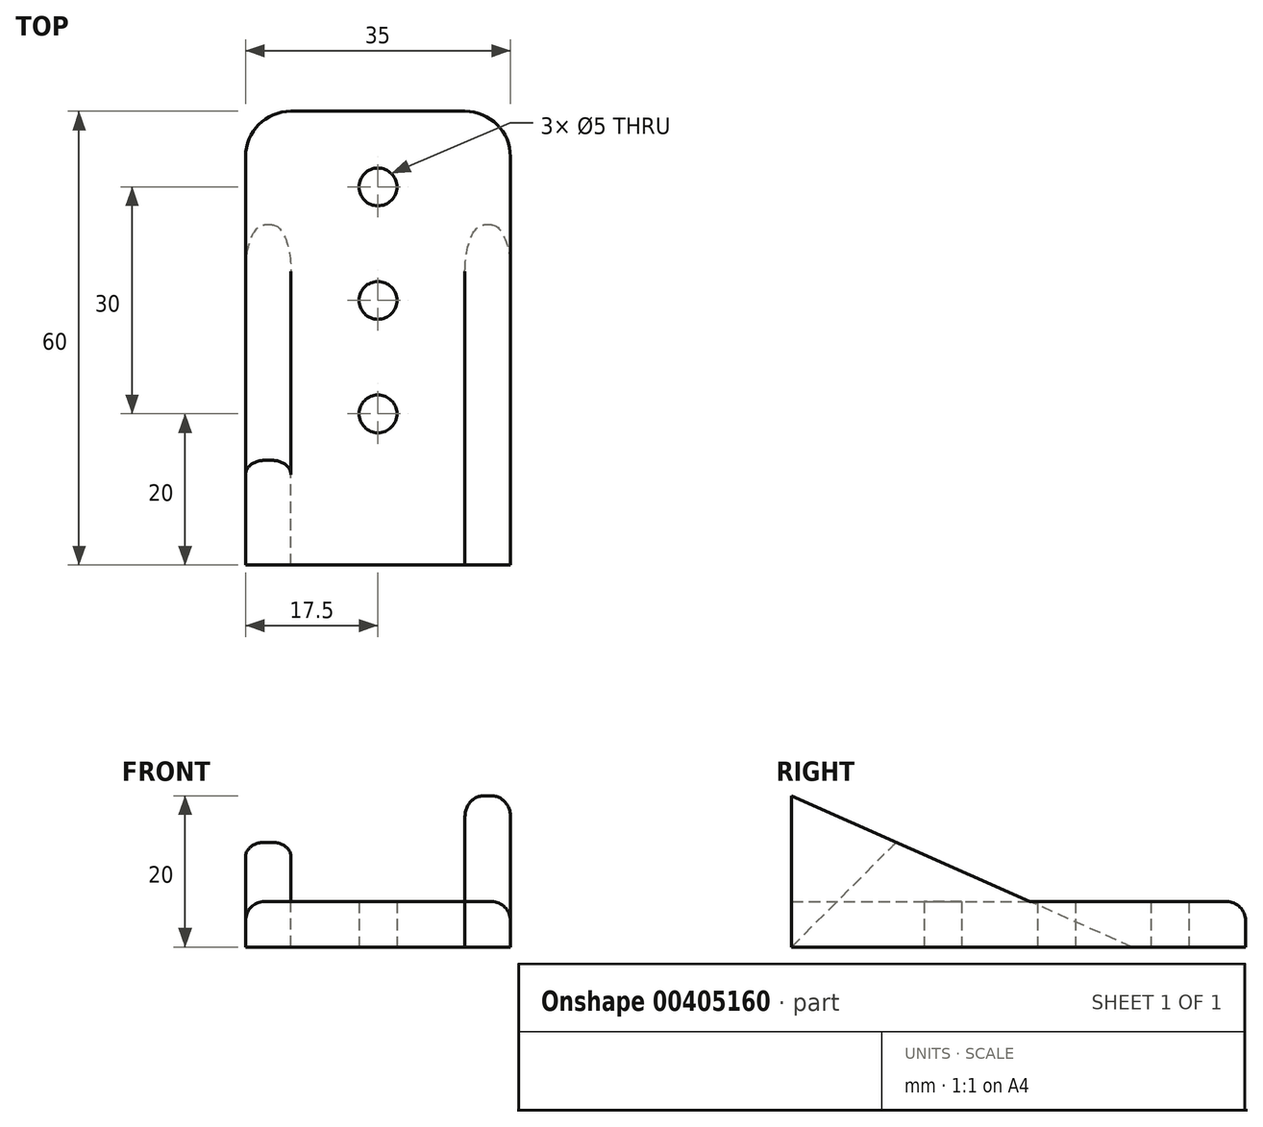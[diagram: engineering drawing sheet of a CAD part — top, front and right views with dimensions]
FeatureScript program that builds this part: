
annotation { "Feature Type Name" : "Feature", "Feature Type Description" : "" }
export const myFeature = defineFeature(function(context is Context, id is Id, definition is map)
    precondition{}
    {
        {
            var Q0;
            Q0=qCreatedBy(makeId("Top.planeOp"),FACE);
            var sketch = newSketch(context, id + "F0", { "sketchPlane" : qUnion([Q0])});
            skLineSegment(sketch, "E0.bottom", {"start": v(17.5, -30) * mm, "end": v(-17.5, -30) * mm});
            skLineSegment(sketch, "E0.top", {"start": v(17.5, 30) * mm, "end": v(-17.5, 30) * mm});
            skLineSegment(sketch, "E0.left", {"start": v(17.5, -30) * mm, "end": v(17.5, 30) * mm});
            skLineSegment(sketch, "E0.right", {"start": v(-17.5, -30) * mm, "end": v(-17.5, 30) * mm});
            skPoint(sketch, "E0.middle", {"position": v(0, 0) * mm});
            skLineSegment(sketch, "E1", {"start": v(0, 0) * mm, "end": v(0, 20) * mm});
            skLineSegment(sketch, "E2", {"start": v(0, 0) * mm, "end": v(0, -10) * mm});
            skCircle(sketch, "E3", {"center": v(0, 20) * mm, "radius": 2.5 * mm});
            skCircle(sketch, "E4", {"center": v(0, -10) * mm, "radius": 2.5 * mm});
            skLineSegment(sketch, "E5", {"start": v(0, 0) * mm, "end": v(0, 5) * mm});
            skCircle(sketch, "E6", {"center": v(0, 5) * mm, "radius": 2.5 * mm});
            skSolve(sketch);
        }
        {
            var Q0;
            Q0 = qSketchRegion(id + "F0", true);
            extrude(context, id + "F1", {"entities" : qUnion([Q0]), "depth" : 6 * mm});
        }
        {
            var Q0;
            Q0=qCreatedBy(makeId("Right.planeOp"),FACE);
            var sketch = newSketch(context, id + "F2", { "sketchPlane" : qUnion([Q0])});
            skLineSegment(sketch, "E7", {"start": v(0, 0) * mm, "end": v(-30, 0) * mm});
            skLineSegment(sketch, "E8", {"start": v(-30, 0) * mm, "end": v(-30, 20) * mm});
            skLineSegment(sketch, "E9", {"start": v(15, 0) * mm, "end": v(0, 0) * mm});
            skLineSegment(sketch, "E10", {"start": v(15, 0) * mm, "end": v(-30, 20) * mm});
            skSolve(sketch);
        }
        {
            var Q0;
            Q0 = qSketchRegion(id + "F2", true);
            extrude(context, id + "F3", {"entities" : qUnion([Q0]), "endBound" : BoundingType.SYMMETRIC, "depth" : 6 * mm});
        }
        {
            var Q0;
            Q0=makeQuery(id+"F3.opExtrude","SWEPT_BODY",BODY,{"disambiguationData":[OSD([sQuery(id+"F2.wireOp",EDGE,"E7"),sQuery(id+"F2.wireOp",EDGE,"E8"),sQuery(id+"F2.wireOp",EDGE,"E9"),sQuery(id+"F2.wireOp",EDGE,"E10")])]});
            transform(context, id + "F4", {"entities" : qUnion([Q0]), "transformType" : TransformType.TRANSLATION_3D, "dx" : 14.5 * mm, "dy" : 0 * mm, "dz" : 0 * mm, "makeCopy" : true});
        }
        {
            var Q0;
            Q0=makeQuery(id+"F3.opExtrude","SWEPT_BODY",BODY,{"disambiguationData":[OSD([sQuery(id+"F2.wireOp",EDGE,"E7"),sQuery(id+"F2.wireOp",EDGE,"E8"),sQuery(id+"F2.wireOp",EDGE,"E9"),sQuery(id+"F2.wireOp",EDGE,"E10")])]});
            transform(context, id + "F5", {"entities" : qUnion([Q0]), "transformType" : TransformType.TRANSLATION_3D, "dx" : -14.5 * mm, "dy" : 0 * mm, "dz" : 0 * mm, "makeCopy" : false});
        }
        {
            var Q0;
            Q0=makeQuery(id+"F1.opExtrude","SWEPT_EDGE",EDGE,{"disambiguationData":[OSD([sQuery(id+"F0.wireOp",EDGE,"E0.top"),sQuery(id+"F0.wireOp",EDGE,"E0.left")])]});
            var Q1;
            Q1=makeQuery(id+"F1.opExtrude","SWEPT_EDGE",EDGE,{"disambiguationData":[OSD([sQuery(id+"F0.wireOp",EDGE,"E0.top"),sQuery(id+"F0.wireOp",EDGE,"E0.right")])]});
            fillet(context, id + "F6", {"entities" : qUnion([Q0, Q1]), "radius" : 6 * mm, "tangentPropagation" : true, "allowEdgeOverflow" : false});
        }
        {
            var Q0;
            Q0=makeQuery(id+"F1.opExtrude","CAP_EDGE",EDGE,{"disambiguationData":[OSD([sQuery(id+"F0.wireOp",EDGE,"E0.left")])],"isStart":false});
            var Q1;
            Q1=makeQuery(id+"F4.opPattern","COPY",EDGE,{"derivedFrom":makeQuery(id+"F3.opExtrude","CAP_EDGE",EDGE,{"disambiguationData":[OSD([sQuery(id+"F2.wireOp",EDGE,"E10")])],"isStart":false}),"instanceName":"1"});
            var Q2;
            Q2=makeQuery(id+"F3.opExtrude","CAP_EDGE",EDGE,{"disambiguationData":[OSD([sQuery(id+"F2.wireOp",EDGE,"E10")])],"isStart":true});
            var Q3;
            Q3=makeQuery(id+"F3.opExtrude","CAP_EDGE",EDGE,{"disambiguationData":[OSD([sQuery(id+"F2.wireOp",EDGE,"E10")])],"isStart":false});
            var Q4;
            Q4=makeQuery(id+"F4.opPattern","COPY",EDGE,{"derivedFrom":makeQuery(id+"F3.opExtrude","CAP_EDGE",EDGE,{"disambiguationData":[OSD([sQuery(id+"F2.wireOp",EDGE,"E10")])],"isStart":true}),"instanceName":"1"});
            fillet(context, id + "F7", {"entities" : qUnion([Q0, Q1, Q2, Q3, Q4]), "radius" : 2.5 * mm, "tangentPropagation" : true, "allowEdgeOverflow" : false});
        }
        {
            var Q0;
            Q0=qCreatedBy(makeId("Right.planeOp"),FACE);
            var sketch = newSketch(context, id + "F8", { "sketchPlane" : qUnion([Q0])});
            skLineSegment(sketch, "E11", {"start": v(0, 0) * mm, "end": v(-30, 0) * mm});
            skLineSegment(sketch, "E12", {"start": v(-30, 0) * mm, "end": v(-18.06, 0) * mm});
            skLineSegment(sketch, "E13", {"start": v(0, 30) * mm, "end": v(-30, 0) * mm});
            skLineSegment(sketch, "E14", {"start": v(0, 30) * mm, "end": v(-30, 30) * mm});
            skLineSegment(sketch, "E15", {"start": v(-30, 30) * mm, "end": v(-30, 0) * mm});
            skSolve(sketch);
        }
        {
            var Q0;
            Q0 = qSketchRegion(id + "F8", true);
            extrude(context, id + "F9", {"entities" : qUnion([Q0]), "endBound" : BoundingType.SYMMETRIC, "depth" : 40 * mm});
        }
        {
            var Q0;
            Q0=makeQuery(id+"F9.opExtrude","SWEPT_BODY",BODY,{"disambiguationData":[OSD([sQuery(id+"F8.wireOp",EDGE,"E13"),sQuery(id+"F8.wireOp",EDGE,"E14"),sQuery(id+"F8.wireOp",EDGE,"E15")])]});
            var Q1;
            Q1=makeQuery(id+"F3.opExtrude","SWEPT_BODY",BODY,{"disambiguationData":[OSD([sQuery(id+"F2.wireOp",EDGE,"E7"),sQuery(id+"F2.wireOp",EDGE,"E8"),sQuery(id+"F2.wireOp",EDGE,"E9"),sQuery(id+"F2.wireOp",EDGE,"E10")])]});
            booleanBodies(context, id + "F10", {"operationType" : BooleanOperationType.SUBTRACTION, "tools" : qUnion([Q0]), "targets" : qUnion([Q1])});
        }
    });
